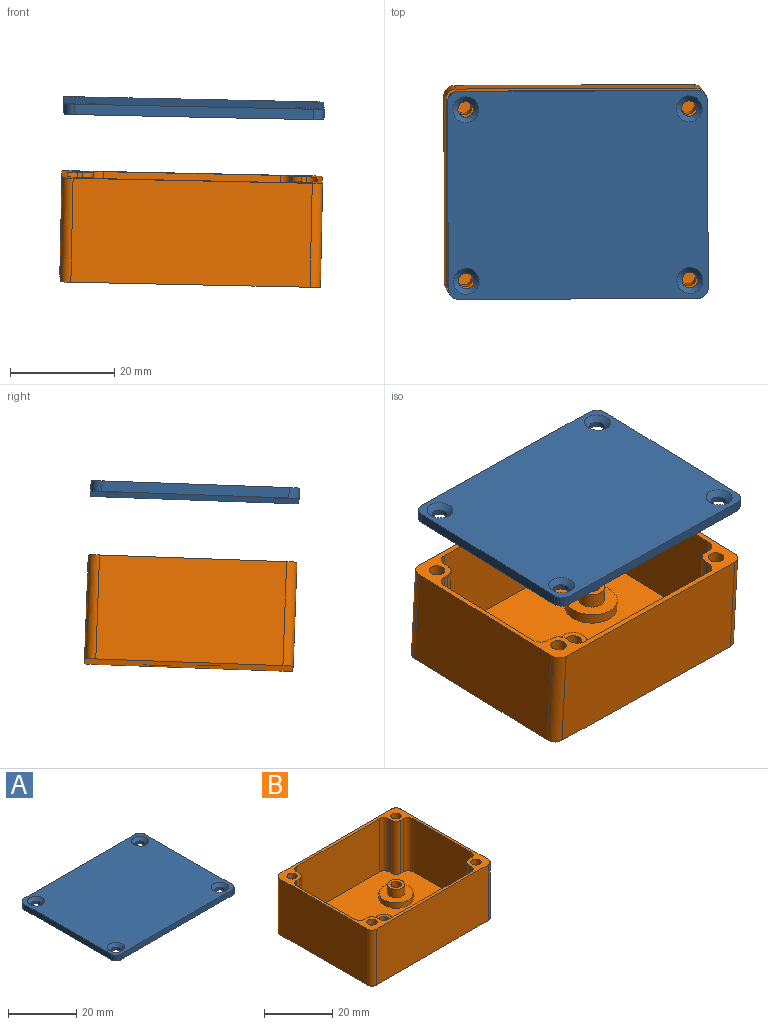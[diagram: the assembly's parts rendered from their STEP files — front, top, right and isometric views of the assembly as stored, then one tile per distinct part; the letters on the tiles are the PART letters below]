
ASSEMBLY  parts=2 mates=1
PART A: 18 faces, bbox 50x40x2 mm
  f0: plane 46x2mm, normal (0,1,0), area 92mm2, adj f4,f5,f14,f17
  f1: plane 36x2mm, normal (-1,0,0), area 72mm2, adj f4,f5,f14,f15
  f2: plane 46x2mm, normal (0,-1,0), area 92mm2, adj f4,f5,f15,f16
  f3: plane 36x2mm, normal (1,0,0), area 72mm2, adj f4,f5,f16,f17
  f4: plane 50x40mm, normal (0,0,1), area 1918mm2, adj f0,f1,f2,f3,f10,f11,f12,f13
  f5: plane 50x40mm, normal (0,0,-1), area 1968.3mm2, adj f0,f1,f2,f3,f6,f7,f8,f9
  f6: cylinder r=1.5mm len=3mm, axis (0,0,1), area 9.4mm2, adj f5,f13
  f7: cylinder r=1.5mm len=3mm, axis (0,0,1), area 9.4mm2, adj f5,f12
  f8: cylinder r=1.5mm len=3mm, axis (0,0,1), area 9.4mm2, adj f5,f11
  f9: cylinder r=1.5mm len=3mm, axis (0,0,1), area 9.4mm2, adj f5,f10
  f10: cone r=1.5mm half-angle=45deg, axis (0,0,1), area 17.8mm2, adj f4,f9
  f11: cone r=1.5mm half-angle=45deg, axis (0,0,1), area 17.8mm2, adj f4,f8
  f12: cone r=1.5mm half-angle=45deg, axis (0,0,1), area 17.8mm2, adj f4,f7
  f13: cone r=1.5mm half-angle=45deg, axis (0,0,1), area 17.8mm2, adj f4,f6
  f14: cylinder r=2mm len=2mm, axis (0,0,1), area 6.3mm2, adj f0,f1,f4,f5
  f15: cylinder r=2mm len=2mm, axis (0,0,-1), area 6.3mm2, adj f1,f2,f4,f5
  f16: cylinder r=2mm len=2mm, axis (0,0,1), area 6.3mm2, adj f2,f3,f4,f5
  f17: cylinder r=2mm len=2mm, axis (0,0,-1), area 6.3mm2, adj f0,f3,f4,f5
PART B: 67 faces, bbox 50x40x20 mm
  f0: plane 50x40mm, normal (0,0,-1), area 1949.8mm2, adj f8,f9,f10,f11,f37,f38,f39,f40
  f1: cylinder r=1.5mm len=4mm, axis (0,0,-1), area 37.7mm2, adj f30,f50
  f2: cylinder r=1.5mm len=4mm, axis (0,0,-1), area 37.7mm2, adj f32,f43
  f3: plane 48x38mm, normal (0,0,1), area 1563.5mm2, adj f4,f5,f6,f7,f13,f14,f15,f16
  f4: plane 34x19mm, normal (0,1,0), area 646mm2, adj f3,f12,f59,f61
  f5: plane 24x19mm, normal (-1,0,0), area 456mm2, adj f3,f12,f62,f63
  f6: plane 34x19mm, normal (0,-1,0), area 646mm2, adj f3,f12,f64,f65
  f7: plane 24x19mm, normal (1,0,0), area 456mm2, adj f3,f12,f60,f66
  f8: plane 46x20mm, normal (0,1,0), area 920mm2, adj f0,f12,f55,f58
  f9: plane 36x20mm, normal (-1,0,0), area 720mm2, adj f0,f12,f55,f56
  f10: plane 46x20mm, normal (0,-1,0), area 920mm2, adj f0,f12,f56,f57
  f11: plane 36x20mm, normal (1,0,0), area 720mm2, adj f0,f12,f57,f58
  f12: plane 50x40mm, normal (0,0,1), area 247.7mm2, adj f4,f5,f6,f7,f8,f9,f10,f11
  f13: plane 19x1mm, normal (0,-1,0), area 19mm2, adj f3,f12,f54,f66
  f14: plane 19x1mm, normal (1,0,0), area 19mm2, adj f3,f12,f54,f65
  f15: plane 19x1mm, normal (0,-1,0), area 19mm2, adj f3,f12,f53,f63
  f16: plane 19x1mm, normal (-1,0,0), area 19mm2, adj f3,f12,f53,f64
  f17: plane 19x1mm, normal (0,1,0), area 19mm2, adj f3,f12,f52,f62
  f18: plane 19x1mm, normal (-1,0,0), area 19mm2, adj f3,f12,f52,f61
  f19: plane 19x1mm, normal (0,1,0), area 19mm2, adj f3,f12,f51,f60
  f20: plane 19x1mm, normal (1,0,0), area 19mm2, adj f3,f12,f51,f59
  f21: cylinder r=1.5mm len=10mm, axis (0,0,1), area 94.2mm2, adj f12,f22
  f22: plane 3x3mm, normal (0,0,1), area 7.1mm2, adj f21
  f23: cylinder r=1.5mm len=10mm, axis (0,0,1), area 94.2mm2, adj f12,f24
  f24: plane 3x3mm, normal (0,0,1), area 7.1mm2, adj f23
  f25: cylinder r=1.5mm len=10mm, axis (0,0,1), area 94.2mm2, adj f12,f26
  f26: plane 3x3mm, normal (0,0,1), area 7.1mm2, adj f25
  f27: cylinder r=1.5mm len=10mm, axis (0,0,1), area 94.2mm2, adj f12,f28
  f28: plane 3x3mm, normal (0,0,1), area 7.1mm2, adj f27
  f29: cylinder r=2.5mm len=5mm, axis (0,0,-1), area 47.1mm2, adj f30,f34
  f30: plane 5x5mm, normal (0,0,1), area 12.6mm2, adj f1,f29
  f31: cylinder r=2.5mm len=5mm, axis (0,0,-1), area 47.1mm2, adj f32,f36
  f32: plane 5x5mm, normal (0,0,1), area 12.6mm2, adj f2,f31
  f33: cylinder r=5mm len=10mm, axis (0,0,-1), area 62.8mm2, adj f3,f34
  f34: plane 10x10mm, normal (0,0,1), area 58.9mm2, adj f29,f33
  f35: cylinder r=5mm len=10mm, axis (0,0,-1), area 62.8mm2, adj f3,f36
  f36: plane 10x10mm, normal (0,0,1), area 58.9mm2, adj f31,f35
  f37: plane 2.6x2mm, normal (-0.87,0.5,0), area 6mm2, adj f0,f38,f42,f43
  f38: plane 3x2mm, normal (0,1,0), area 6mm2, adj f0,f37,f39,f43
  f39: plane 2.6x2mm, normal (0.87,0.5,0), area 6mm2, adj f0,f38,f40,f43
  f40: plane 2.6x2mm, normal (0.87,-0.5,0), area 6mm2, adj f0,f39,f41,f43
  f41: plane 3x2mm, normal (0,-1,0), area 6mm2, adj f0,f40,f42,f43
  f42: plane 2.6x2mm, normal (-0.87,-0.5,0), area 6mm2, adj f0,f37,f41,f43
  f43: plane 6x5.2mm, normal (0,0,-1), area 16.3mm2, adj f2,f37,f38,f39,f40,f41,f42
  f44: plane 2.6x2mm, normal (-0.87,-0.5,0), area 6mm2, adj f0,f45,f49,f50
  f45: plane 2.6x2mm, normal (-0.87,0.5,0), area 6mm2, adj f0,f44,f46,f50
  f46: plane 3x2mm, normal (0,1,0), area 6mm2, adj f0,f45,f47,f50
  f47: plane 2.6x2mm, normal (0.87,0.5,0), area 6mm2, adj f0,f46,f48,f50
  f48: plane 2.6x2mm, normal (0.87,-0.5,0), area 6mm2, adj f0,f47,f49,f50
  f49: plane 3x2mm, normal (0,-1,0), area 6mm2, adj f0,f44,f48,f50
  f50: plane 6x5.2mm, normal (0,0,-1), area 16.3mm2, adj f1,f44,f45,f46,f47,f48,f49
  f51: cylinder r=2mm len=19mm, axis (0,0,1), area 59.7mm2, adj f3,f12,f19,f20
  f52: cylinder r=2mm len=19mm, axis (0,0,1), area 59.7mm2, adj f3,f12,f17,f18
  f53: cylinder r=2mm len=19mm, axis (0,0,1), area 59.7mm2, adj f3,f12,f15,f16
  f54: cylinder r=2mm len=19mm, axis (0,0,1), area 59.7mm2, adj f3,f12,f13,f14
  f55: cylinder r=2mm len=20mm, axis (0,0,1), area 62.8mm2, adj f0,f8,f9,f12
  f56: cylinder r=2mm len=20mm, axis (0,0,-1), area 62.8mm2, adj f0,f9,f10,f12
  f57: cylinder r=2mm len=20mm, axis (0,0,1), area 62.8mm2, adj f0,f10,f11,f12
  f58: cylinder r=2mm len=20mm, axis (0,0,-1), area 62.8mm2, adj f0,f8,f11,f12
  f59: cylinder r=2mm len=19mm, axis (0,0,1), area 59.7mm2, adj f3,f4,f12,f20
  f60: cylinder r=2mm len=19mm, axis (0,0,-1), area 59.7mm2, adj f3,f7,f12,f19
  f61: cylinder r=2mm len=19mm, axis (0,0,-1), area 59.7mm2, adj f3,f4,f12,f18
  f62: cylinder r=2mm len=19mm, axis (0,0,1), area 59.7mm2, adj f3,f5,f12,f17
  f63: cylinder r=2mm len=19mm, axis (0,0,-1), area 59.7mm2, adj f3,f5,f12,f15
  f64: cylinder r=2mm len=19mm, axis (0,0,1), area 59.7mm2, adj f3,f6,f12,f16
  f65: cylinder r=2mm len=19mm, axis (0,0,-1), area 59.7mm2, adj f3,f6,f12,f14
  f66: cylinder r=2mm len=19mm, axis (0,0,1), area 59.7mm2, adj f3,f7,f12,f13
PLACE A rot(axis=(0.86,0.51,0.09),2.4deg) t=(-5.57,10.23,33.05)mm
PLACE B rot(axis=(0.86,0.51,0.09),2.4deg) t=(77.63,10.4,-1)mm
MATE slider B.f25 <-> A.f8  axis (0.02,-0.04,1) through (63.22,24.57,19.83)mm
